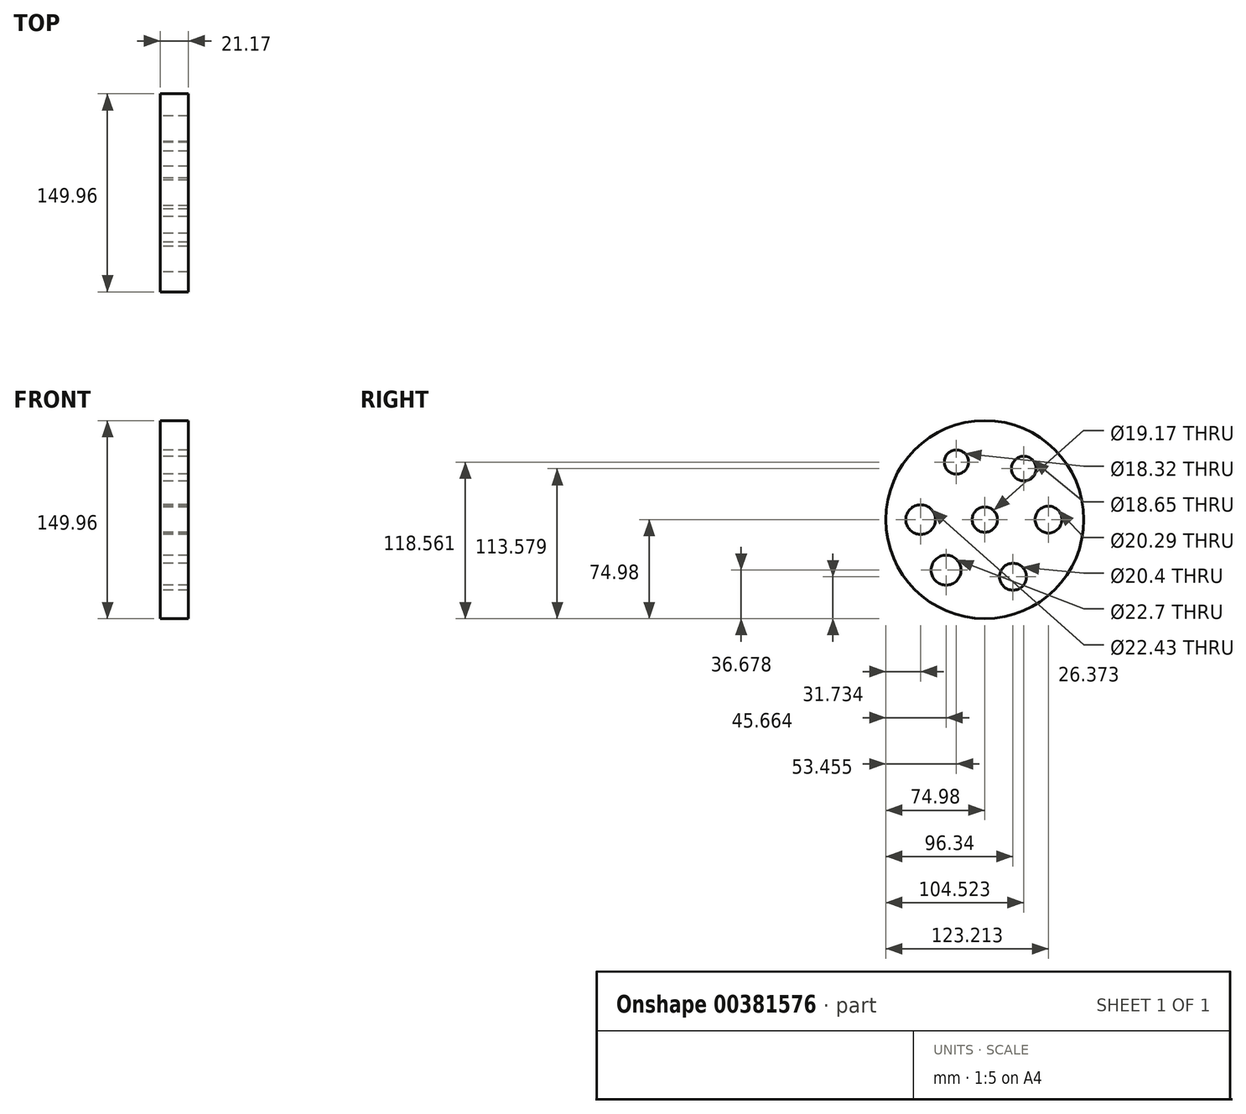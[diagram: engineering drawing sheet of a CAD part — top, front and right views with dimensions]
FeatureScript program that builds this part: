
annotation { "Feature Type Name" : "Feature", "Feature Type Description" : "" }
export const myFeature = defineFeature(function(context is Context, id is Id, definition is map)
    precondition{}
    {
        {
            var Q0;
            Q0=qCreatedBy(makeId("Right.planeOp"),FACE);
            var sketch = newSketch(context, id + "F0", { "sketchPlane" : qUnion([Q0])});
            skCircle(sketch, "E0", {"center": v(0, 0) * mm, "radius": 74.98 * mm});
            skCircle(sketch, "E1", {"center": v(0, 0) * mm, "radius": 9.59 * mm});
            skPoint(sketch, "E2", {"position": v(-48.6, 0) * mm});
            skPoint(sketch, "E3", {"position": v(48.23, 0) * mm});
            skPoint(sketch, "E4.1.0", {"position": v(21.36, -43.25) * mm});
            skPoint(sketch, "E4.1.1", {"position": v(-21.53, 43.58) * mm});
            skPoint(sketch, "E4.2.0", {"position": v(-29.32, -38.3) * mm});
            skPoint(sketch, "E4.2.1", {"position": v(29.54, 38.6) * mm});
            skLineSegment(sketch, "E4.anchor1", {"start": v(0, 0) * mm, "end": v(-48.6, 0) * mm, "construction": true});
            skLineSegment(sketch, "E4.anchor2", {"start": v(0, 0) * mm, "end": v(29.54, 38.6) * mm, "construction": true});
            skCircle(sketch, "E5", {"center": v(-21.53, 43.58) * mm, "radius": 0.86 * mm});
            skCircle(sketch, "E6", {"center": v(-21.53, 43.58) * mm, "radius": 9.16 * mm});
            skCircle(sketch, "E7", {"center": v(29.54, 38.6) * mm, "radius": 9.33 * mm});
            skCircle(sketch, "E8", {"center": v(48.23, 0) * mm, "radius": 10.15 * mm});
            skCircle(sketch, "E9", {"center": v(21.36, -43.25) * mm, "radius": 10.2 * mm});
            skCircle(sketch, "E10", {"center": v(-29.32, -38.3) * mm, "radius": 11.35 * mm});
            skCircle(sketch, "E11", {"center": v(-48.6, 0) * mm, "radius": 11.21 * mm});
            skSolve(sketch);
        }
        {
            var Q0;
            Q0=makeQuery(id+"F0.imprint","IMPRINT",FACE,{"disambiguationData":[TD([[makeQuery(id+"F0.imprint","IMPRINT",EDGE,{"derivedFrom":sQuery(id+"F0.wireOp",EDGE,"E0")}),1.0]])]});
            extrude(context, id + "F1", {"entities" : qUnion([Q0]), "depth" : 21.17 * mm});
        }
        {
            var Q0;
            Q0=qCreatedBy(makeId("Front.planeOp"),FACE);
            var sketch = newSketch(context, id + "F2", { "sketchPlane" : qUnion([Q0])});
            skLineSegment(sketch, "E12", {"start": v(21.14, 76.06) * mm, "end": v(21.14, -76.01) * mm});
            skLineSegment(sketch, "E13", {"start": v(0, 76.05) * mm, "end": v(0, -75.95) * mm});
            skPoint(sketch, "E14", {"position": v(0, 76.05) * mm});
            skPoint(sketch, "E15", {"position": v(2.66, 76.05) * mm});
            skPoint(sketch, "E16", {"position": v(18.66, 75.97) * mm});
            skArc(sketch, "E17", {"start": v(2.66, 76.05) * mm, "mid": v(10.6, 66.37) * mm, "end": v(18.66, 75.97) * mm});
            skLineSegment(sketch, "E18", {"start": v(0, 76.05) * mm, "end": v(2.66, 76.05) * mm});
            skPoint(sketch, "E19", {"position": v(0, -75.95) * mm});
            skPoint(sketch, "E20", {"position": v(3.28, -75.95) * mm});
            skPoint(sketch, "E21", {"position": v(17.4, -75.9) * mm});
            skArc(sketch, "E22", {"start": v(17.4, -75.9) * mm, "mid": v(10.31, -68.3) * mm, "end": v(3.28, -75.95) * mm});
            skLineSegment(sketch, "E23", {"start": v(0, -75.95) * mm, "end": v(3.28, -75.95) * mm});
            skLineSegment(sketch, "E24", {"start": v(17.4, -75.9) * mm, "end": v(21.14, -76.01) * mm});
            skLineSegment(sketch, "E25", {"start": v(18.66, 75.97) * mm, "end": v(21.14, 76.06) * mm});
            skSolve(sketch);
        }
    });
